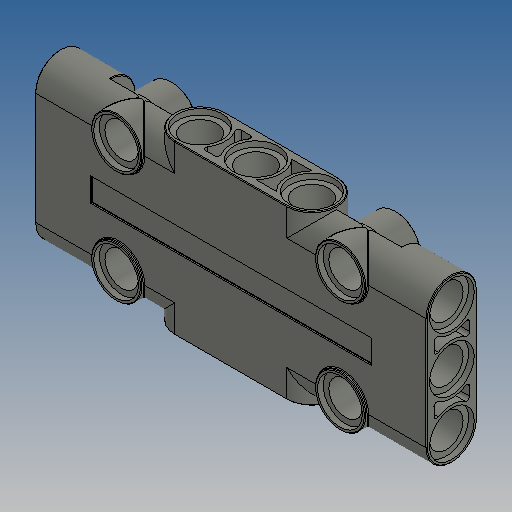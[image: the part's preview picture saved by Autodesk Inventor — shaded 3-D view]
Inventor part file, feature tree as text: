
AUTODESK INVENTOR PART (.ipt)
format: ipt  version: 2025 (Build 290162010, 162A)  size: 1,121,792 bytes
history: native  units: in
note: dims shown in document units (in); Inventor stores cm internally (conversion verified against a paired STEP export)
features: extrude x16, sketch x11, mirror x3, plane x1, fillet x1
ambient origin geometry x8: Origin, YZ Plane, XZ Plane, XY Plane, X Axis, Y Axis, Z Axis, Center Point
bodies: Solid1 (feature_tree)
feature tree (32):
  extrude  "Extrusion1"  Depth=0.189in
  sketch  "Sketch3"  dims[d4=2.2047in d5=0.0in]
  extrude  "Extrusion2"  Depth=0.0315in
  extrude  "Extrusion3"  TaperAngle=0.0deg  [1 undecoded]
  extrude  "Extrusion4"  Depth=0.252in
  plane  "Work Plane1"
  extrude  "Extrusion5"  Depth=0.315in
  sketch  "Sketch5"  dims[d12=0.3937in d14=0.3937in d16=0.2835in]
  extrude  "Extrusion6"  Depth=0.2835in
  extrude  "Extrusion7"  Depth=0.0315in
  extrude  "Extrusion10"  Depth=0.2205in TaperAngle=0.0deg
  extrude  "Extrusion8"  Depth=0.189in
  extrude  "Extrusion9"  Depth=0.0315in TaperAngle=0.0deg
  mirror  "Mirror1"
  mirror  "Mirror2"
  sketch  "Sketch8"  dims[d22=-0.1417in d23=0.189in]
  extrude  "Extrusion11"  Depth=0.189in
  extrude  "Extrusion12"  Depth=0.3937in
  extrude  "Extrusion13"  Depth=0.2677in
  sketch  "Sketch9"  dims[d24=0.2835in d25=0.0315in d26=0.0in]
  extrude  "Extrusion14"  TaperAngle=0.0deg  [1 undecoded]
  extrude  "Extrusion16"  Depth=0.2677in TaperAngle=0.0deg
  mirror  "Mirror3"
  extrude  "Extrusion15"  Depth=0.252in
  fillet  "Fillet1"  Radius=0.0315in
  sketch  "Sketch2"  dims[d2=0.2835in d3=0.0315in]
  sketch  "Skizze - Rechteckige Anordnung1"  dims[d0=0.315in d1=0.189in]
  sketch  "Sketch4"  dims[d8=45.0deg d9=0.7874in d11=0.315in]
  sketch  "Sketch6"  dims[d17=0.0in d18=0.0315in]
  sketch  "Sketch7"  dims[d19=0.0in d20=0.2205in d21=0.0in]
  sketch  "Sketch10"  dims[d27=0.2835in d28=0.189in d29=0.6299in d30=0.2677in d31=0.0472in d32=0.0in d33=0.0in d34=0.2677in d35=0.0in d36=0.252in d37=0.0315in d38=0.0in d39=0.252in d40=0.0315in d41=0.0in d42=0.0315in d43=0.2205in d44=0.0in d45=0.2835in d46=0.6299in d47=0.189in d48=0.1417in d49=0.1417in d50=0.0in d51=0.0in d52=0.1417in d53=0.0in d54=0.315in d55=0.0in d56=0.252in d57=0.0315in d58=0.0in d59=1.5748in d60=0.126in d62=0.0079in d63=0.0in d64=45.0deg d72=0.2205in d73=0.0in d74=0.0039in d75=0.0157in d76=0.7874in d78=0.315in d79=0.3937in d81=0.3937in]
  sketch  "Skizze - Rechteckige Anordnung3"  dims[d6=0.189in d7=0.252in]
note: 2 required parameter values undecoded (feature->parameter linkage not recoverable at this tier; creation-order binding heuristic only, values carry confidence <= 0.55)
